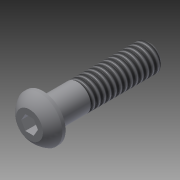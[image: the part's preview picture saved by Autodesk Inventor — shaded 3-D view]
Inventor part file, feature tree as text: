
AUTODESK INVENTOR PART (.ipt)
format: ipt  version: 2015 (Build 190159000, 159)  size: 118,784 bytes
history: native  units: in
note: dims shown in document units (in); Inventor stores cm internally (conversion verified against a paired STEP export)
features: sketch x2, revolve x1, chamfer x1, extrude x1, thread x1
ambient origin geometry x8: Origin, YZ Plane, XZ Plane, XY Plane, X Axis, Y Axis, Z Axis, Center Point
bodies: Solid1 (feature_tree)
feature tree (6):
  revolve  "Revolution1"  [1 undecoded]
  chamfer  "Chamfer1"  Distance=0.125in
  extrude  "Extrusion1"  TaperAngle=90.0deg  [1 undecoded]
  thread  "Thread1"  [1 undecoded]
  sketch  "Sketch1"  dims[d0=0.125in d1=0.211in]
  sketch  "Sketch2"  dims[d2=0.031in d3=0.125in d7=90.0deg d8=0.125in d9=0.236in d10=0.03in d11=0.125in d12=45.0deg d14=0.1562in d15=0.111in d16=0.0in d17=0.65in d18=0.0in d20=1.0in]
note: 3 required parameter values undecoded (feature->parameter linkage not recoverable at this tier; creation-order binding heuristic only, values carry confidence <= 0.55)